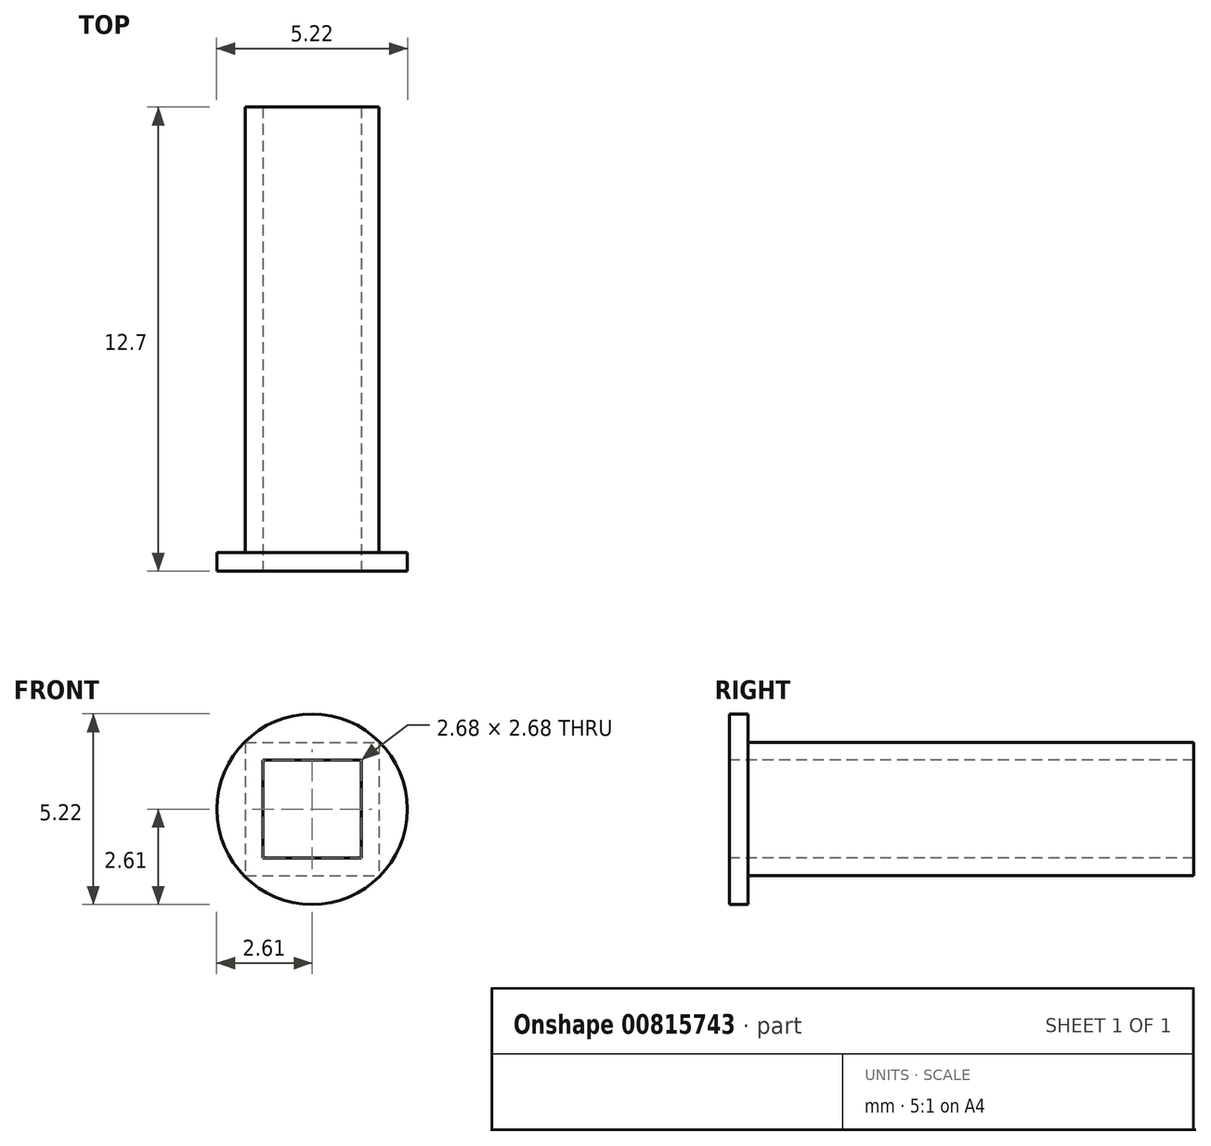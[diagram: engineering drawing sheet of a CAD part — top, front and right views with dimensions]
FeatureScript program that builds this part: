
annotation { "Feature Type Name" : "Feature", "Feature Type Description" : "" }
export const myFeature = defineFeature(function(context is Context, id is Id, definition is map)
    precondition{}
    {
        {
            var Q0;
            Q0=qCreatedBy(makeId("Front.planeOp"),FACE);
            var sketch = newSketch(context, id + "F0", { "sketchPlane" : qUnion([Q0])});
            skLineSegment(sketch, "E0.bottom", {"start": v(0, 0) * mm, "end": v(1.82, 0) * mm});
            skLineSegment(sketch, "E0.top", {"start": v(0, -1.82) * mm, "end": v(1.82, -1.82) * mm});
            skLineSegment(sketch, "E0.left", {"start": v(0, 0) * mm, "end": v(0, -1.82) * mm});
            skLineSegment(sketch, "E0.right", {"start": v(1.82, 0) * mm, "end": v(1.82, -1.82) * mm});
            skSolve(sketch);
        }
        {
            var Q0;
            Q0=makeQuery(id+"F0.imprint","IMPRINT",FACE,{"disambiguationData":[TD([[makeQuery(id+"F0.imprint","IMPRINT",EDGE,{"derivedFrom":sQuery(id+"F0.wireOp",EDGE,"E0.bottom")}),-1.0]])]});
            extrude(context, id + "F1", {"entities" : qUnion([Q0]), "oppositeDirection" : true, "depth" : 12.7 * mm, "offsetDistance" : 25.4 * mm});
        }
        {
            var Q0;
            Q0=makeQuery(id+"F1.opExtrude","CAP_FACE",FACE,{"disambiguationData":[OSD([sQuery(id+"F0.wireOp",EDGE,"E0.bottom"),sQuery(id+"F0.wireOp",EDGE,"E0.top"),sQuery(id+"F0.wireOp",EDGE,"E0.left"),sQuery(id+"F0.wireOp",EDGE,"E0.right")])],"isStart":true});
            var Q1;
            Q1=makeQuery(id+"F1.opExtrude","SWEPT_FACE",FACE,{"disambiguationData":[OSD([sQuery(id+"F0.wireOp",EDGE,"E0.left")])]});
            var Q2;
            Q2=makeQuery(id+"F1.opExtrude","SWEPT_FACE",FACE,{"disambiguationData":[OSD([sQuery(id+"F0.wireOp",EDGE,"E0.bottom")])]});
            var Q3;
            Q3=makeQuery(id+"F1.opExtrude","CAP_FACE",FACE,{"disambiguationData":[OSD([sQuery(id+"F0.wireOp",EDGE,"E0.bottom"),sQuery(id+"F0.wireOp",EDGE,"E0.top"),sQuery(id+"F0.wireOp",EDGE,"E0.left"),sQuery(id+"F0.wireOp",EDGE,"E0.right")])],"isStart":false});
            shell(context, id + "F2", {"entities" : qUnion([Q0, Q1, Q2, Q3]), "thickness" : 0.48 * mm});
        }
        {
            var Q0;
            Q0=makeQuery(id+"F2.opShell","OFFSET_EDGE",EDGE,{"disambiguationData":[OSD([sQuery(id+"F0.wireOp",EDGE,"E0.bottom"),sQuery(id+"F0.wireOp",EDGE,"E0.right")])]});
            cPoint(context, id + "F3", {"entities" : qUnion([Q0]), "parameter" : 0.5});
        }
        {
            var Q0;
            Q0=makeQuery(id+"F1.opExtrude","SWEPT_BODY",BODY,{"disambiguationData":[OSD([sQuery(id+"F0.wireOp",EDGE,"E0.bottom"),sQuery(id+"F0.wireOp",EDGE,"E0.top"),sQuery(id+"F0.wireOp",EDGE,"E0.left"),sQuery(id+"F0.wireOp",EDGE,"E0.right")])]});
            var Q1;
            Q1=makeQuery(id+"F1.opExtrude","SWEPT_EDGE",EDGE,{"disambiguationData":[OSD([sQuery(id+"F0.wireOp",EDGE,"E0.bottom"),sQuery(id+"F0.wireOp",EDGE,"E0.right")])]});
            var Q2;
            Q2 = qCreatedBy(id + "F3" ,VERTEX);
            var Q3;
            Q3=makeQuery(id+"F1.opExtrude","SWEPT_FACE",FACE,{"disambiguationData":[OSD([sQuery(id+"F0.wireOp",EDGE,"E0.bottom")])]});
            transform(context, id + "F4", {"entities" : qUnion([Q0]), "transformType" : TransformType.TRANSLATION_DISTANCE, "transformDirection" : qUnion([Q2, Q3]), "distance" : 1.83 * mm, "makeCopy" : true});
        }
        {
            var Q0;
            Q0=makeQuery(id+"F4.opPattern","COPY",BODY,{"derivedFrom":makeQuery(id+"F1.opExtrude","SWEPT_BODY",BODY,{"disambiguationData":[OSD([sQuery(id+"F0.wireOp",EDGE,"E0.bottom"),sQuery(id+"F0.wireOp",EDGE,"E0.top"),sQuery(id+"F0.wireOp",EDGE,"E0.left"),sQuery(id+"F0.wireOp",EDGE,"E0.right")])]}),"instanceName":"1"});
            var Q1;
            Q1=makeQuery(id+"F4.opPattern","COPY",EDGE,{"derivedFrom":makeQuery(id+"F2.opShell","OFFSET_EDGE",EDGE,{"disambiguationData":[OSD([sQuery(id+"F0.wireOp",EDGE,"E0.top"),sQuery(id+"F0.wireOp",EDGE,"E0.left")])]}),"instanceName":"1"});
            transform(context, id + "F5", {"entities" : qUnion([Q0]), "transformType" : TransformType.ROTATION, "transformAxis" : qUnion([Q1]), "angle" : 90 * degree, "makeCopy" : false});
        }
        {
            var Q0;
            Q0=makeQuery(id+"F4.opPattern","COPY",BODY,{"derivedFrom":makeQuery(id+"F1.opExtrude","SWEPT_BODY",BODY,{"disambiguationData":[OSD([sQuery(id+"F0.wireOp",EDGE,"E0.bottom"),sQuery(id+"F0.wireOp",EDGE,"E0.top"),sQuery(id+"F0.wireOp",EDGE,"E0.left"),sQuery(id+"F0.wireOp",EDGE,"E0.right")])]}),"instanceName":"1"});
            transform(context, id + "F6", {"entities" : qUnion([Q0]), "transformType" : TransformType.TRANSLATION_3D, "dx" : 1.34 * mm, "dy" : 0 * mm, "dz" : -0.5 * mm, "makeCopy" : false});
        }
        {
            var Q0;
            Q0=makeQuery(id+"F4.opPattern","COPY",BODY,{"derivedFrom":makeQuery(id+"F1.opExtrude","SWEPT_BODY",BODY,{"disambiguationData":[OSD([sQuery(id+"F0.wireOp",EDGE,"E0.bottom"),sQuery(id+"F0.wireOp",EDGE,"E0.top"),sQuery(id+"F0.wireOp",EDGE,"E0.left"),sQuery(id+"F0.wireOp",EDGE,"E0.right")])]}),"instanceName":"1"});
            deleteBodies(context, id + "F7", {"entities" : qUnion([Q0])});
        }
        {
            var Q0;
            Q0=makeQuery(id+"F1.opExtrude","SWEPT_BODY",BODY,{"disambiguationData":[OSD([sQuery(id+"F0.wireOp",EDGE,"E0.bottom"),sQuery(id+"F0.wireOp",EDGE,"E0.top"),sQuery(id+"F0.wireOp",EDGE,"E0.left"),sQuery(id+"F0.wireOp",EDGE,"E0.right")])]});
            var Q1;
            Q1=qCreatedBy(makeId("Top.planeOp"),FACE);
            mirror(context, id + "F8", {"operationType" : NewBodyOperationType.ADD, "entities" : qUnion([Q0]), "mirrorPlane" : qUnion([Q1])});
        }
        {
            var Q0;
            Q0=makeQuery(id+"F1.opExtrude","SWEPT_BODY",BODY,{"disambiguationData":[OSD([sQuery(id+"F0.wireOp",EDGE,"E0.bottom"),sQuery(id+"F0.wireOp",EDGE,"E0.top"),sQuery(id+"F0.wireOp",EDGE,"E0.left"),sQuery(id+"F0.wireOp",EDGE,"E0.right")])]});
            var Q1;
            Q1=qCreatedBy(makeId("Right.planeOp"),FACE);
            mirror(context, id + "F9", {"operationType" : NewBodyOperationType.ADD, "entities" : qUnion([Q0]), "mirrorPlane" : qUnion([Q1])});
        }
        {
            var Q0;
            {var subQ0=makeQuery(id+"F1.opExtrude","CAP_FACE",FACE,{"disambiguationData":[OSD([sQuery(id+"F0.wireOp",EDGE,"E0.bottom"),sQuery(id+"F0.wireOp",EDGE,"E0.top"),sQuery(id+"F0.wireOp",EDGE,"E0.left"),sQuery(id+"F0.wireOp",EDGE,"E0.right")])],"isStart":true});var subQ1=makeQuery(id+"F8.boolean.opBoolean","MERGE",FACE,{"derivedFrom":[subQ0,makeQuery(id+"F8.opPattern","COPY",FACE,{"derivedFrom":subQ0,"instanceName":"1"})]});Q0=makeQuery(id+"F9.boolean.opBoolean","MERGE",FACE,{"derivedFrom":[subQ1,makeQuery(id+"F9.opPattern","COPY",FACE,{"derivedFrom":subQ1,"instanceName":"1"})]});}
            var sketch = newSketch(context, id + "F10", { "sketchPlane" : qUnion([Q0])});
            skCircle(sketch, "E1", {"center": v(0, 0) * mm, "radius": 2.6 * mm});
            skSolve(sketch);
        }
        {
            var Q0;
            Q0=makeQuery(id+"F10.imprint","IMPRINT",FACE,{"disambiguationData":[TD([[makeQuery(id+"F10.imprint","IMPRINT",EDGE,{"derivedFrom":sQuery(id+"F10.wireOp",EDGE,"E1")}),1.0]])]});
            extrude(context, id + "F11", {"entities" : qUnion([Q0]), "depth" : 0.25 * mm, "offsetDistance" : 25.4 * mm});
        }
        {
            var Q0;
            Q0=makeQuery(id+"F11.opExtrude","SWEPT_BODY",BODY,{"disambiguationData":[OSD([sQuery(id+"F0.wireOp",EDGE,"E0.top"),sQuery(id+"F0.wireOp",EDGE,"E0.right"),sQuery(id+"F10.wireOp",EDGE,"E1")])]});
            transform(context, id + "F12", {"entities" : qUnion([Q0]), "transformType" : TransformType.TRANSLATION_3D, "dx" : 0 * mm, "dy" : 0.5 * mm, "dz" : 0 * mm, "makeCopy" : false});
        }
        {
            var Q0;
            Q0=makeQuery(id+"F11.opExtrude","SWEPT_BODY",BODY,{"disambiguationData":[OSD([sQuery(id+"F0.wireOp",EDGE,"E0.top"),sQuery(id+"F0.wireOp",EDGE,"E0.right"),sQuery(id+"F10.wireOp",EDGE,"E1")])]});
            var Q1;
            Q1=makeQuery(id+"F11.opExtrude","CAP_FACE",FACE,{"disambiguationData":[OSD([sQuery(id+"F0.wireOp",EDGE,"E0.top"),sQuery(id+"F0.wireOp",EDGE,"E0.right"),sQuery(id+"F10.wireOp",EDGE,"E1")])],"isStart":false});
            mirror(context, id + "F13", {"operationType" : NewBodyOperationType.ADD, "entities" : qUnion([Q0]), "mirrorPlane" : qUnion([Q1])});
        }
    });
